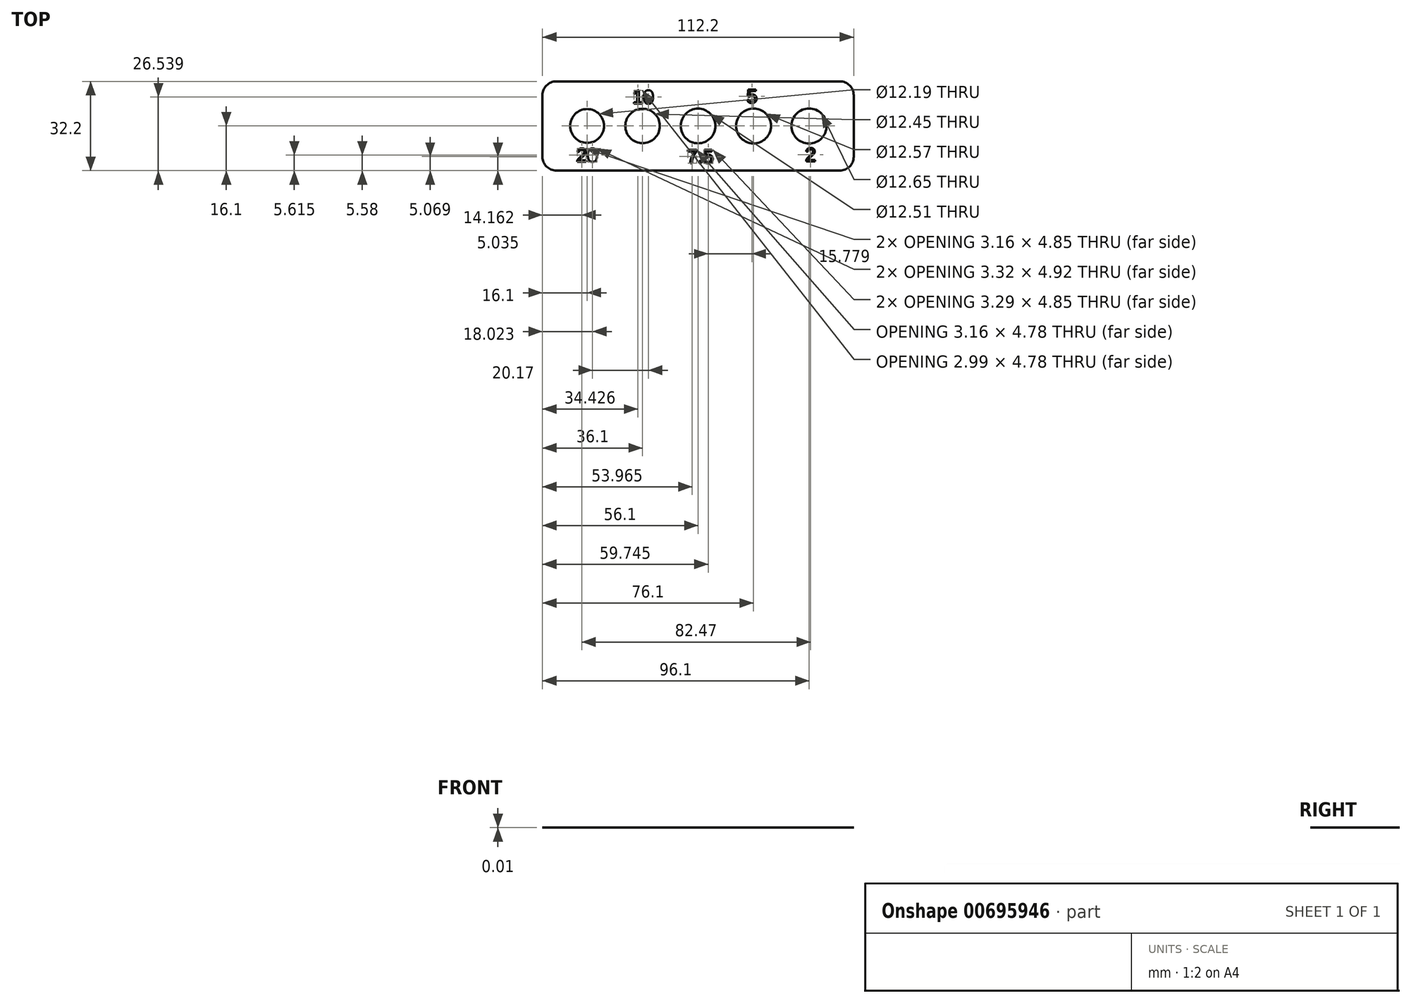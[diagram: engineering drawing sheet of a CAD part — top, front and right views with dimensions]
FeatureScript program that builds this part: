
annotation { "Feature Type Name" : "Feature", "Feature Type Description" : "" }
export const myFeature = defineFeature(function(context is Context, id is Id, definition is map)
    precondition{}
    {
        {
            var Q0;
            Q0=qCreatedBy(makeId("Top.planeOp"),FACE);
            var sketch = newSketch(context, id + "F0", { "sketchPlane" : qUnion([Q0])});
            skCircle(sketch, "E0", {"center": v(-40, 0) * mm, "radius": 6.1 * mm});
            skCircle(sketch, "E1", {"center": v(-20, 0) * mm, "radius": 6.22 * mm});
            skCircle(sketch, "E2", {"center": v(20, 0) * mm, "radius": 6.29 * mm});
            skCircle(sketch, "E3", {"center": v(40, 0) * mm, "radius": 6.32 * mm});
            skCircle(sketch, "E4", {"center": v(0, 0) * mm, "radius": 6.25 * mm});
            skLineSegment(sketch, "E5", {"start": v(-40, 0) * mm, "end": v(-20, 0) * mm, "construction": true});
            skLineSegment(sketch, "E6", {"start": v(-20, 0) * mm, "end": v(0, 0) * mm, "construction": true});
            skLineSegment(sketch, "E7", {"start": v(0, 0) * mm, "end": v(20, 0) * mm, "construction": true});
            skLineSegment(sketch, "E8", {"start": v(20, 0) * mm, "end": v(40, 0) * mm, "construction": true});
            skLineSegment(sketch, "E9.bottom", {"start": v(56.1, -16.1) * mm, "end": v(-56.1, -16.1) * mm});
            skLineSegment(sketch, "E9.top", {"start": v(56.1, 16.1) * mm, "end": v(-56.1, 16.1) * mm});
            skLineSegment(sketch, "E9.left", {"start": v(56.1, -16.1) * mm, "end": v(56.1, 16.1) * mm});
            skLineSegment(sketch, "E9.right", {"start": v(-56.1, -16.1) * mm, "end": v(-56.1, 16.1) * mm});
            skText(sketch, "E10", { "text": "20", "fontName": "Arimo-Regular.ttf"});
            skText(sketch, "E11", { "text": "10", "fontName": "Arimo-Regular.ttf"});
            skText(sketch, "E12", { "text": "7.5", "fontName": "Arimo-Regular.ttf"});
            skText(sketch, "E13", { "text": "5", "fontName": "Arimo-Regular.ttf"});
            skText(sketch, "E14", { "text": "2", "fontName": "Arimo-Regular.ttf"});
            const initialGuessF0  = {"E10": [-0.04387, -0.01291, 1, 0, 0.005], "E11": [-0.0237, 0.00805, 1, 0, 0.005], "E12": [-0.00407, -0.01342, 1, 0, 0.005], "E13": [0.0175, 0.00833, 1, 0, 0.005], "E14": [0.0386, -0.01277, 1, 0, 0.005]};
            skSetInitialGuess(sketch, initialGuessF0);
            skSolve(sketch);
        }
        {
            var Q0;
            Q0 = qSketchRegion(id + "F0", true);
            extrude(context, id + "F1", {"entities" : qUnion([Q0]), "depth" : 3 / 406.4 * mm, "offsetDistance" : 25 * mm});
        }
        {
            var Q0;
            Q0=makeQuery(id+"F1.opExtrude","SWEPT_EDGE",EDGE,{"disambiguationData":[OSD([sQuery(id+"F0.wireOp",EDGE,"E9.bottom"),sQuery(id+"F0.wireOp",EDGE,"E9.right")])]});
            var Q1;
            Q1=makeQuery(id+"F1.opExtrude","SWEPT_EDGE",EDGE,{"disambiguationData":[OSD([sQuery(id+"F0.wireOp",EDGE,"E9.top"),sQuery(id+"F0.wireOp",EDGE,"E9.right")])]});
            var Q2;
            Q2=makeQuery(id+"F1.opExtrude","SWEPT_EDGE",EDGE,{"disambiguationData":[OSD([sQuery(id+"F0.wireOp",EDGE,"E9.top"),sQuery(id+"F0.wireOp",EDGE,"E9.left")])]});
            var Q3;
            Q3=makeQuery(id+"F1.opExtrude","SWEPT_EDGE",EDGE,{"disambiguationData":[OSD([sQuery(id+"F0.wireOp",EDGE,"E9.bottom"),sQuery(id+"F0.wireOp",EDGE,"E9.left")])]});
            fillet(context, id + "F2", {"entities" : qUnion([Q0, Q1, Q2, Q3]), "radius" : 5 * mm, "tangentPropagation" : true, "allowEdgeOverflow" : false});
        }
    });
